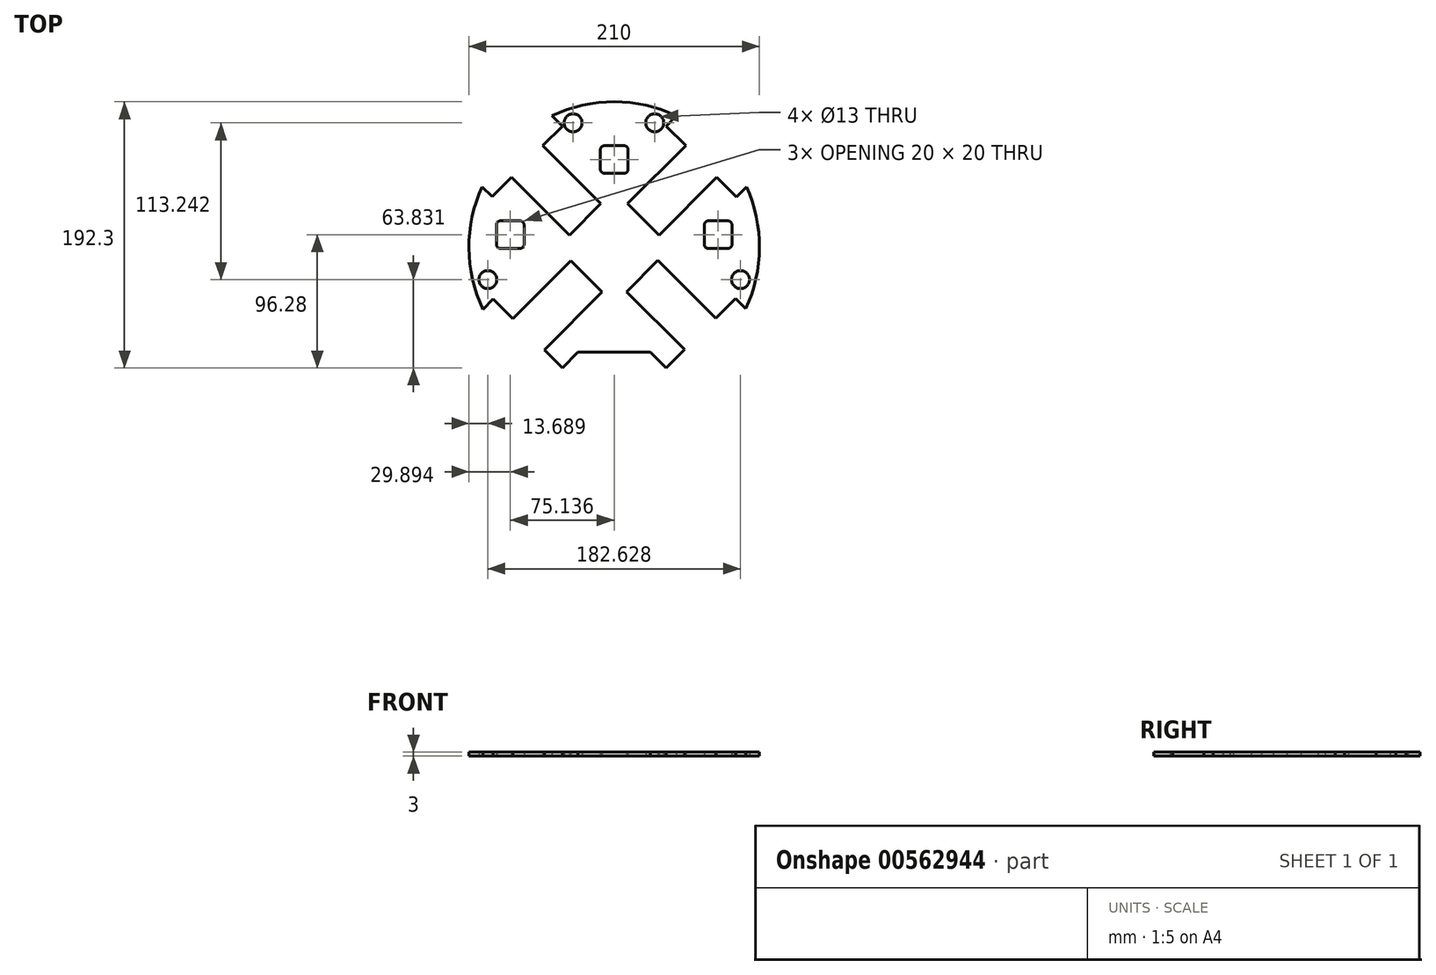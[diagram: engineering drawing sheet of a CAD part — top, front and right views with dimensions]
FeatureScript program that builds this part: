
annotation { "Feature Type Name" : "Feature", "Feature Type Description" : "" }
export const myFeature = defineFeature(function(context is Context, id is Id, definition is map)
    precondition{}
    {
        {
            var Q0;
            Q0=qCreatedBy(makeId("Top.planeOp"),FACE);
            var sketch = newSketch(context, id + "F0", { "sketchPlane" : qUnion([Q0])});
            skCircle(sketch, "E0", {"center": v(-0.03, 1.02) * mm, "radius": 105 * mm});
            skCircle(sketch, "E1", {"center": v(-29.75, 90.8) * mm, "radius": 6.5 * mm});
            skCircle(sketch, "E2", {"center": v(29.27, 90.8) * mm, "radius": 6.5 * mm});
            skCircle(sketch, "E3", {"center": v(-91.34, -22.45) * mm, "radius": 6.5 * mm});
            skCircle(sketch, "E4", {"center": v(91.29, -22.45) * mm, "radius": 6.5 * mm});
            skLineSegment(sketch, "E5", {"start": v(-26.15, -74.78) * mm, "end": v(26.1, -74.78) * mm});
            skLineSegment(sketch, "E6", {"start": v(-26.15, -74.78) * mm, "end": v(-45.16, -93.79) * mm});
            skLineSegment(sketch, "E7", {"start": v(26.1, -74.78) * mm, "end": v(45.1, -93.79) * mm});
            skLineSegment(sketch, "E8", {"start": v(0, 0) * mm, "end": v(104.97, 0) * mm});
            skLineSegment(sketch, "E9.left", {"start": v(0, 0) * mm, "end": v(0, 103.03) * mm});
            skLineSegment(sketch, "E10.left", {"start": v(0, 0) * mm, "end": v(0, 104.98) * mm});
            skLineSegment(sketch, "E11", {"start": v(-20.96, 21.1) * mm, "end": v(-32.26, 9.77) * mm});
            skLineSegment(sketch, "E12", {"start": v(-20.96, 21.1) * mm, "end": v(-9.66, 32.42) * mm});
            skLineSegment(sketch, "E13", {"start": v(21, 21) * mm, "end": v(9.68, 32.31) * mm});
            skLineSegment(sketch, "E14", {"start": v(9.68, 32.31) * mm, "end": v(32.31, 9.68) * mm});
            skLineSegment(sketch, "E15", {"start": v(-20, -20) * mm, "end": v(-31.32, -8.7) * mm});
            skLineSegment(sketch, "E16", {"start": v(-20, -20) * mm, "end": v(-8.7, -31.32) * mm});
            skLineSegment(sketch, "E17", {"start": v(20.08, -19.9) * mm, "end": v(31.34, -8.52) * mm});
            skLineSegment(sketch, "E18", {"start": v(31.34, -8.52) * mm, "end": v(20.08, -19.9) * mm});
            skLineSegment(sketch, "E19", {"start": v(20.08, -19.9) * mm, "end": v(8.82, -31.26) * mm});
            skLineSegment(sketch, "E20", {"start": v(-0.03, 1.02) * mm, "end": v(0, -74.78) * mm});
            skLineSegment(sketch, "E21.bottom", {"start": v(-82.14, 0) * mm, "end": v(-68.14, 0) * mm});
            skLineSegment(sketch, "E21.top", {"start": v(-82.14, 20) * mm, "end": v(-68.14, 20) * mm});
            skLineSegment(sketch, "E21.left", {"start": v(-85.14, 3) * mm, "end": v(-85.14, 17) * mm});
            skLineSegment(sketch, "E21.right", {"start": v(-65.14, 3) * mm, "end": v(-65.14, 17) * mm});
            skLineSegment(sketch, "E22.bottom", {"start": v(82.1, 0) * mm, "end": v(68.1, 0) * mm});
            skLineSegment(sketch, "E22.top", {"start": v(82.1, 20) * mm, "end": v(68.1, 20) * mm});
            skLineSegment(sketch, "E22.left", {"start": v(85.1, 3) * mm, "end": v(85.1, 17) * mm});
            skLineSegment(sketch, "E22.right", {"start": v(65.1, 3) * mm, "end": v(65.1, 17) * mm});
            skPoint(sketch, "E23.visualSharp", {"position": v(-85.14, 20) * mm});
            skArc(sketch, "E23.filletArc", {"start": v(-82.14, 20) * mm, "mid": v(-84.26, 19.12) * mm, "end": v(-85.14, 17) * mm});
            skPoint(sketch, "E24.visualSharp", {"position": v(-65.14, 20) * mm});
            skArc(sketch, "E24.filletArc", {"start": v(-65.14, 17) * mm, "mid": v(-66.01, 19.12) * mm, "end": v(-68.14, 20) * mm});
            skPoint(sketch, "E25.visualSharp", {"position": v(-65.14, 0) * mm});
            skArc(sketch, "E25.filletArc", {"start": v(-68.14, 0) * mm, "mid": v(-66.01, 0.88) * mm, "end": v(-65.14, 3) * mm});
            skPoint(sketch, "E26.visualSharp", {"position": v(-85.14, 0) * mm});
            skArc(sketch, "E26.filletArc", {"start": v(-85.14, 3) * mm, "mid": v(-84.26, 0.88) * mm, "end": v(-82.14, 0) * mm});
            skPoint(sketch, "E27.visualSharp", {"position": v(65.1, 0) * mm});
            skArc(sketch, "E27.filletArc", {"start": v(65.1, 3) * mm, "mid": v(65.98, 0.88) * mm, "end": v(68.1, 0) * mm});
            skPoint(sketch, "E28.visualSharp", {"position": v(65.1, 20) * mm});
            skArc(sketch, "E28.filletArc", {"start": v(68.1, 20) * mm, "mid": v(65.98, 19.12) * mm, "end": v(65.1, 17) * mm});
            skPoint(sketch, "E29.visualSharp", {"position": v(85.1, 20) * mm});
            skArc(sketch, "E29.filletArc", {"start": v(85.1, 17) * mm, "mid": v(84.23, 19.12) * mm, "end": v(82.1, 20) * mm});
            skPoint(sketch, "E30.visualSharp", {"position": v(85.1, 0) * mm});
            skArc(sketch, "E30.filletArc", {"start": v(82.1, 0) * mm, "mid": v(84.23, 0.88) * mm, "end": v(85.1, 3) * mm});
            skLineSegment(sketch, "E31", {"start": v(50.85, -72.9) * mm, "end": v(37.6, -86.28) * mm});
            skLineSegment(sketch, "E32", {"start": v(73.53, -50.31) * mm, "end": v(87.6, -36.1) * mm});
            skLineSegment(sketch, "E33", {"start": v(87.6, -36.1) * mm, "end": v(95.07, -43.5) * mm});
            skLineSegment(sketch, "E34", {"start": v(50.85, -72.9) * mm, "end": v(8.82, -31.26) * mm});
            skLineSegment(sketch, "E35", {"start": v(31.34, -8.52) * mm, "end": v(73.53, -50.31) * mm});
            skLineSegment(sketch, "E36", {"start": v(-50.53, -73.16) * mm, "end": v(-37.53, -86.16) * mm});
            skLineSegment(sketch, "E37", {"start": v(-73.32, -50.69) * mm, "end": v(-87.46, -36.55) * mm});
            skLineSegment(sketch, "E38", {"start": v(-87.46, -36.55) * mm, "end": v(-94.9, -43.98) * mm});
            skLineSegment(sketch, "E39", {"start": v(-73.32, -50.69) * mm, "end": v(-31.32, -8.7) * mm});
            skLineSegment(sketch, "E40", {"start": v(-8.7, -31.32) * mm, "end": v(-50.53, -73.16) * mm});
            skLineSegment(sketch, "E41", {"start": v(-74.16, 51.56) * mm, "end": v(-88.28, 37.4) * mm});
            skLineSegment(sketch, "E42", {"start": v(-88.28, 37.4) * mm, "end": v(-95.54, 44.64) * mm});
            skLineSegment(sketch, "E43", {"start": v(-51.69, 74.34) * mm, "end": v(-37.56, 88.5) * mm});
            skLineSegment(sketch, "E44", {"start": v(-37.56, 88.5) * mm, "end": v(-44.98, 95.9) * mm});
            skLineSegment(sketch, "E45", {"start": v(-51.69, 74.34) * mm, "end": v(-9.66, 32.42) * mm});
            skLineSegment(sketch, "E46", {"start": v(-74.16, 51.56) * mm, "end": v(-32.26, 9.77) * mm});
            skLineSegment(sketch, "E47", {"start": v(51.68, 74.3) * mm, "end": v(37.54, 88.45) * mm});
            skPoint(sketch, "E48.endSnap0", {"position": v(44.6, 81.38) * mm});
            skPoint(sketch, "E49.endSnap0", {"position": v(0, 51.52) * mm});
            skLineSegment(sketch, "E50", {"start": v(74.14, 51.52) * mm, "end": v(88.29, 37.38) * mm});
            skLineSegment(sketch, "E51", {"start": v(51.68, 74.3) * mm, "end": v(9.68, 32.31) * mm});
            skLineSegment(sketch, "E52", {"start": v(74.14, 51.52) * mm, "end": v(32.31, 9.68) * mm});
            skLineSegment(sketch, "E53", {"start": v(0, 74.3) * mm, "end": v(7, 74.3) * mm});
            skLineSegment(sketch, "E54", {"start": v(10, 71.3) * mm, "end": v(10, 57.3) * mm});
            skLineSegment(sketch, "E55", {"start": v(7, 54.3) * mm, "end": v(-7, 54.3) * mm});
            skLineSegment(sketch, "E56", {"start": v(-10, 57.3) * mm, "end": v(-10, 71.3) * mm});
            skLineSegment(sketch, "E57", {"start": v(-7, 74.3) * mm, "end": v(0, 74.3) * mm});
            skPoint(sketch, "E58.visualSharp", {"position": v(-10, 74.3) * mm});
            skArc(sketch, "E58.filletArc", {"start": v(-7, 74.3) * mm, "mid": v(-9.12, 73.43) * mm, "end": v(-10, 71.3) * mm});
            skPoint(sketch, "E59.visualSharp", {"position": v(10, 74.3) * mm});
            skArc(sketch, "E59.filletArc", {"start": v(10, 71.3) * mm, "mid": v(9.12, 73.43) * mm, "end": v(7, 74.3) * mm});
            skPoint(sketch, "E60.visualSharp", {"position": v(10, 54.3) * mm});
            skArc(sketch, "E60.filletArc", {"start": v(7, 54.3) * mm, "mid": v(9.12, 55.18) * mm, "end": v(10, 57.3) * mm});
            skPoint(sketch, "E61.visualSharp", {"position": v(-10, 54.3) * mm});
            skArc(sketch, "E61.filletArc", {"start": v(-10, 57.3) * mm, "mid": v(-9.12, 55.18) * mm, "end": v(-7, 54.3) * mm});
            skLineSegment(sketch, "E62", {"start": v(32.31, 9.68) * mm, "end": v(74.14, 51.52) * mm});
            skLineSegment(sketch, "E63", {"start": v(88.29, 37.38) * mm, "end": v(95.5, 44.6) * mm});
            skLineSegment(sketch, "E64", {"start": v(37.54, 88.45) * mm, "end": v(44.97, 95.88) * mm});
            skSolve(sketch);
        }
        {
            var Q0;
            Q0=makeQuery(id+"F0.imprint","IMPRINT",FACE,{"disambiguationData":[TD([[makeQuery(id+"F0.imprint","IMPRINT",EDGE,{"derivedFrom":sQuery(id+"F0.wireOp",EDGE,"E1")}),-1.0]])]});
            extrude(context, id + "F1", {"entities" : qUnion([Q0]), "depth" : 3 * mm, "offsetDistance" : 25.4 * mm});
        }
    });
